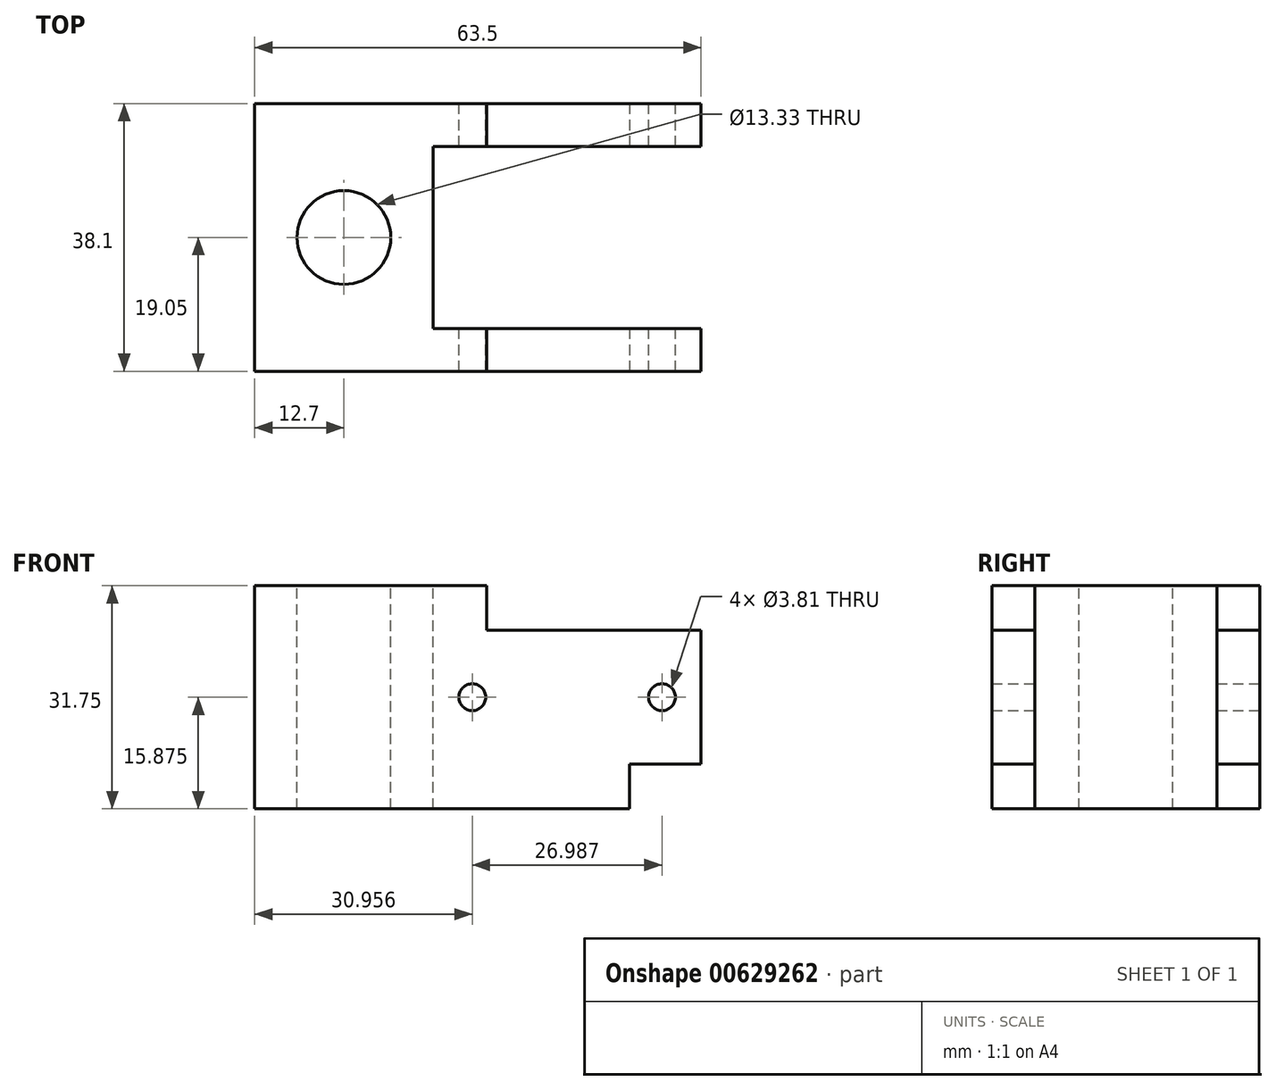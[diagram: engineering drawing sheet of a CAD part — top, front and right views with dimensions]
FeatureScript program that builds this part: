
annotation { "Feature Type Name" : "Feature", "Feature Type Description" : "" }
export const myFeature = defineFeature(function(context is Context, id is Id, definition is map)
    precondition{}
    {
        {
            var Q0;
            Q0=qCreatedBy(makeId("Top.planeOp"),FACE);
            var sketch = newSketch(context, id + "F0", { "sketchPlane" : qUnion([Q0])});
            skLineSegment(sketch, "E0.bottom", {"start": v(12.7, -19.05) * mm, "end": v(-12.7, -19.05) * mm});
            skLineSegment(sketch, "E0.top", {"start": v(12.7, 19.05) * mm, "end": v(-12.7, 19.05) * mm});
            skLineSegment(sketch, "E0.left", {"start": v(12.7, -19.05) * mm, "end": v(12.7, 19.05) * mm});
            skLineSegment(sketch, "E0.right", {"start": v(-12.7, -19.05) * mm, "end": v(-12.7, 19.05) * mm});
            skPoint(sketch, "E0.middle", {"position": v(0, 0) * mm});
            skSolve(sketch);
        }
        {
            var Q0;
            Q0=makeQuery(id+"F0.imprint","IMPRINT",FACE,{"disambiguationData":[TD([[makeQuery(id+"F0.imprint","IMPRINT",EDGE,{"derivedFrom":sQuery(id+"F0.wireOp",EDGE,"E0.bottom")}),-1.0]])]});
            extrude(context, id + "F1", {"entities" : qUnion([Q0]), "depth" : 31.75 * mm, "offsetDistance" : 25.4 * mm});
        }
        {
            var Q0;
            Q0=makeQuery(id+"F1.opExtrude","SWEPT_FACE",FACE,{"disambiguationData":[OSD([sQuery(id+"F0.wireOp",EDGE,"E0.left")])]});
            var sketch = newSketch(context, id + "F2", { "sketchPlane" : qUnion([Q0])});
            skLineSegment(sketch, "E1.bottom", {"start": v(-19.05, 0) * mm, "end": v(-12.95, 0) * mm});
            skLineSegment(sketch, "E1.top", {"start": v(-19.05, 31.75) * mm, "end": v(-12.95, 31.75) * mm});
            skLineSegment(sketch, "E1.left", {"start": v(-19.05, 0) * mm, "end": v(-19.05, 31.75) * mm});
            skLineSegment(sketch, "E1.right", {"start": v(-12.95, 0) * mm, "end": v(-12.95, 31.75) * mm});
            skLineSegment(sketch, "E2.bottom", {"start": v(19.05, 0) * mm, "end": v(12.95, 0) * mm});
            skLineSegment(sketch, "E2.top", {"start": v(19.05, 31.75) * mm, "end": v(12.95, 31.75) * mm});
            skLineSegment(sketch, "E2.left", {"start": v(19.05, 0) * mm, "end": v(19.05, 31.75) * mm});
            skLineSegment(sketch, "E2.right", {"start": v(12.95, 0) * mm, "end": v(12.95, 31.75) * mm});
            skSolve(sketch);
        }
        {
            var Q0;
            Q0=qSketchRegion(id+"F2",true);
            extrude(context, id + "F3", {"entities" : qUnion([Q0]), "operationType" : NewBodyOperationType.ADD, "depth" : 38.1 * mm, "offsetDistance" : 25.4 * mm});
        }
        {
            var Q0;
            Q0=makeQuery(id+"F3.boolean.opBoolean","MERGE",FACE,{"derivedFrom":[makeQuery(id+"F1.opExtrude","CAP_FACE",FACE,{"disambiguationData":[OSD([sQuery(id+"F0.wireOp",EDGE,"E0.bottom"),sQuery(id+"F0.wireOp",EDGE,"E0.top"),sQuery(id+"F0.wireOp",EDGE,"E0.left"),sQuery(id+"F0.wireOp",EDGE,"E0.right")])],"isStart":false}),makeQuery(id+"F3.opExtrude","SWEPT_FACE",FACE,{"disambiguationData":[OSD([sQuery(id+"F2.wireOp",EDGE,"E1.top")])]}),makeQuery(id+"F3.opExtrude","SWEPT_FACE",FACE,{"disambiguationData":[OSD([sQuery(id+"F2.wireOp",EDGE,"E2.top")])]})]});
            var sketch = newSketch(context, id + "F4", { "sketchPlane" : qUnion([Q0])});
            skCircle(sketch, "E3", {"center": v(0, 0) * mm, "radius": 6.67 * mm});
            skSolve(sketch);
        }
        {
            var Q0;
            Q0=qSketchRegion(id+"F4",true);
            extrude(context, id + "F5", {"entities" : qUnion([Q0]), "operationType" : NewBodyOperationType.REMOVE, "endBound" : BoundingType.THROUGH_ALL, "oppositeDirection" : true, "depth" : 25.4 * mm, "offsetDistance" : 25.4 * mm});
        }
        {
            var Q0;
            Q0=makeQuery(id+"F3.boolean.opBoolean","MERGE",FACE,{"derivedFrom":[makeQuery(id+"F1.opExtrude","SWEPT_FACE",FACE,{"disambiguationData":[OSD([sQuery(id+"F0.wireOp",EDGE,"E0.top")])]}),makeQuery(id+"F3.opExtrude","SWEPT_FACE",FACE,{"disambiguationData":[OSD([sQuery(id+"F2.wireOp",EDGE,"E2.left")])]})]});
            var sketch = newSketch(context, id + "F6", { "sketchPlane" : qUnion([Q0])});
            skCircle(sketch, "E4", {"center": v(-45.24, 15.88) * mm, "radius": 1.9 * mm});
            skCircle(sketch, "E5", {"center": v(-18.26, 15.88) * mm, "radius": 1.9 * mm});
            skSolve(sketch);
        }
        {
            var Q0;
            Q0=qSketchRegion(id+"F6",true);
            extrude(context, id + "F7", {"entities" : qUnion([Q0]), "operationType" : NewBodyOperationType.REMOVE, "endBound" : BoundingType.THROUGH_ALL, "oppositeDirection" : true, "depth" : 25.4 * mm, "offsetDistance" : 25.4 * mm});
        }
        {
            var Q0;
            Q0=makeQuery(id+"F3.boolean.opBoolean","MERGE",FACE,{"derivedFrom":[makeQuery(id+"F1.opExtrude","SWEPT_FACE",FACE,{"disambiguationData":[OSD([sQuery(id+"F0.wireOp",EDGE,"E0.bottom")])]}),makeQuery(id+"F3.opExtrude","SWEPT_FACE",FACE,{"disambiguationData":[OSD([sQuery(id+"F2.wireOp",EDGE,"E1.left")])]})]});
            var sketch = newSketch(context, id + "F8", { "sketchPlane" : qUnion([Q0])});
            skLineSegment(sketch, "E6.bottom", {"start": v(50.8, 0) * mm, "end": v(40.64, 0) * mm});
            skLineSegment(sketch, "E6.top", {"start": v(50.8, 6.35) * mm, "end": v(40.64, 6.35) * mm});
            skLineSegment(sketch, "E6.left", {"start": v(50.8, 0) * mm, "end": v(50.8, 6.35) * mm});
            skLineSegment(sketch, "E6.right", {"start": v(40.64, 0) * mm, "end": v(40.64, 6.35) * mm});
            skLineSegment(sketch, "E7.bottom", {"start": v(50.8, 31.75) * mm, "end": v(20.32, 31.75) * mm});
            skLineSegment(sketch, "E7.top", {"start": v(50.8, 25.4) * mm, "end": v(20.32, 25.4) * mm});
            skLineSegment(sketch, "E7.left", {"start": v(50.8, 31.75) * mm, "end": v(50.8, 25.4) * mm});
            skLineSegment(sketch, "E7.right", {"start": v(20.32, 31.75) * mm, "end": v(20.32, 25.4) * mm});
            skSolve(sketch);
        }
        {
            var Q0;
            Q0 = qSketchRegion(id + "F8", true);
            extrude(context, id + "F9", {"entities" : qUnion([Q0]), "operationType" : NewBodyOperationType.REMOVE, "endBound" : BoundingType.THROUGH_ALL, "oppositeDirection" : true, "depth" : 25.4 * mm, "offsetDistance" : 25.4 * mm});
        }
    });
